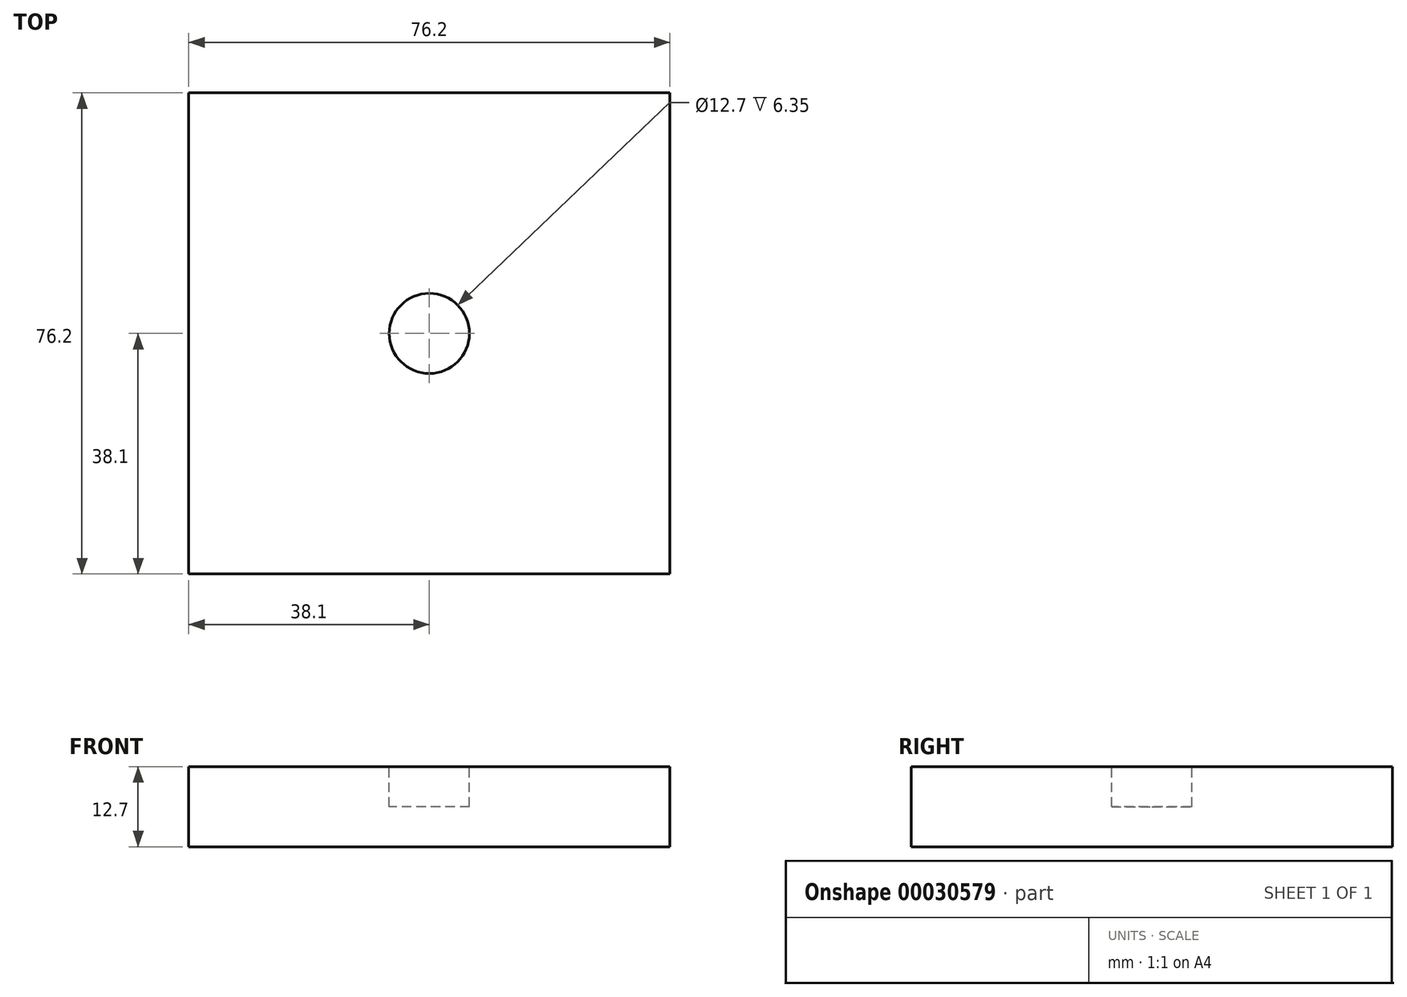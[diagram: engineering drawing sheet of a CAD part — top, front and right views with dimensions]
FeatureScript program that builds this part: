
annotation { "Feature Type Name" : "Feature", "Feature Type Description" : "" }
export const myFeature = defineFeature(function(context is Context, id is Id, definition is map)
    precondition{}
    {
        {
            var Q0;
            Q0=qCreatedBy(makeId("Top.planeOp"),FACE);
            var sketch = newSketch(context, id + "F0", { "sketchPlane" : qUnion([Q0])});
            skLineSegment(sketch, "E0.rect.bottom", {"start": v(-38.1, 38.1) * mm, "end": v(38.1, 38.1) * mm});
            skLineSegment(sketch, "E0.rect.top", {"start": v(-38.1, -38.1) * mm, "end": v(38.1, -38.1) * mm});
            skLineSegment(sketch, "E0.rect.left", {"start": v(-38.1, 38.1) * mm, "end": v(-38.1, -38.1) * mm});
            skLineSegment(sketch, "E0.rect.right", {"start": v(38.1, 38.1) * mm, "end": v(38.1, -38.1) * mm});
            skPoint(sketch, "E0.rect.middle", {"position": v(0, 0) * mm});
            skSolve(sketch);
        }
        {
            var Q0;
            Q0 = qSketchRegion(id + "F0", true);
            extrude(context, id + "F1", {"entities" : qUnion([Q0]), "endBound" : BoundingType.SYMMETRIC, "depth" : 12.7 * mm});
        }
        {
            var Q0;
            Q0=makeQuery(id+"F1.opExtrude","CAP_FACE",FACE,{"disambiguationData":[OSD([sQuery(id+"F0.wireOp",EDGE,"E0.rect.bottom"),sQuery(id+"F0.wireOp",EDGE,"E0.rect.top"),sQuery(id+"F0.wireOp",EDGE,"E0.rect.left"),sQuery(id+"F0.wireOp",EDGE,"E0.rect.right")])],"isStart":false});
            var sketch = newSketch(context, id + "F2", { "sketchPlane" : qUnion([Q0])});
            skCircle(sketch, "E1", {"center": v(0, 0) * mm, "radius": 6.35 * mm});
            skSolve(sketch);
        }
        {
            var Q0;
            Q0 = qSketchRegion(id + "F2", true);
            extrude(context, id + "F3", {"entities" : qUnion([Q0]), "operationType" : NewBodyOperationType.REMOVE, "oppositeDirection" : true, "depth" : 6.35 * mm});
        }
    });
